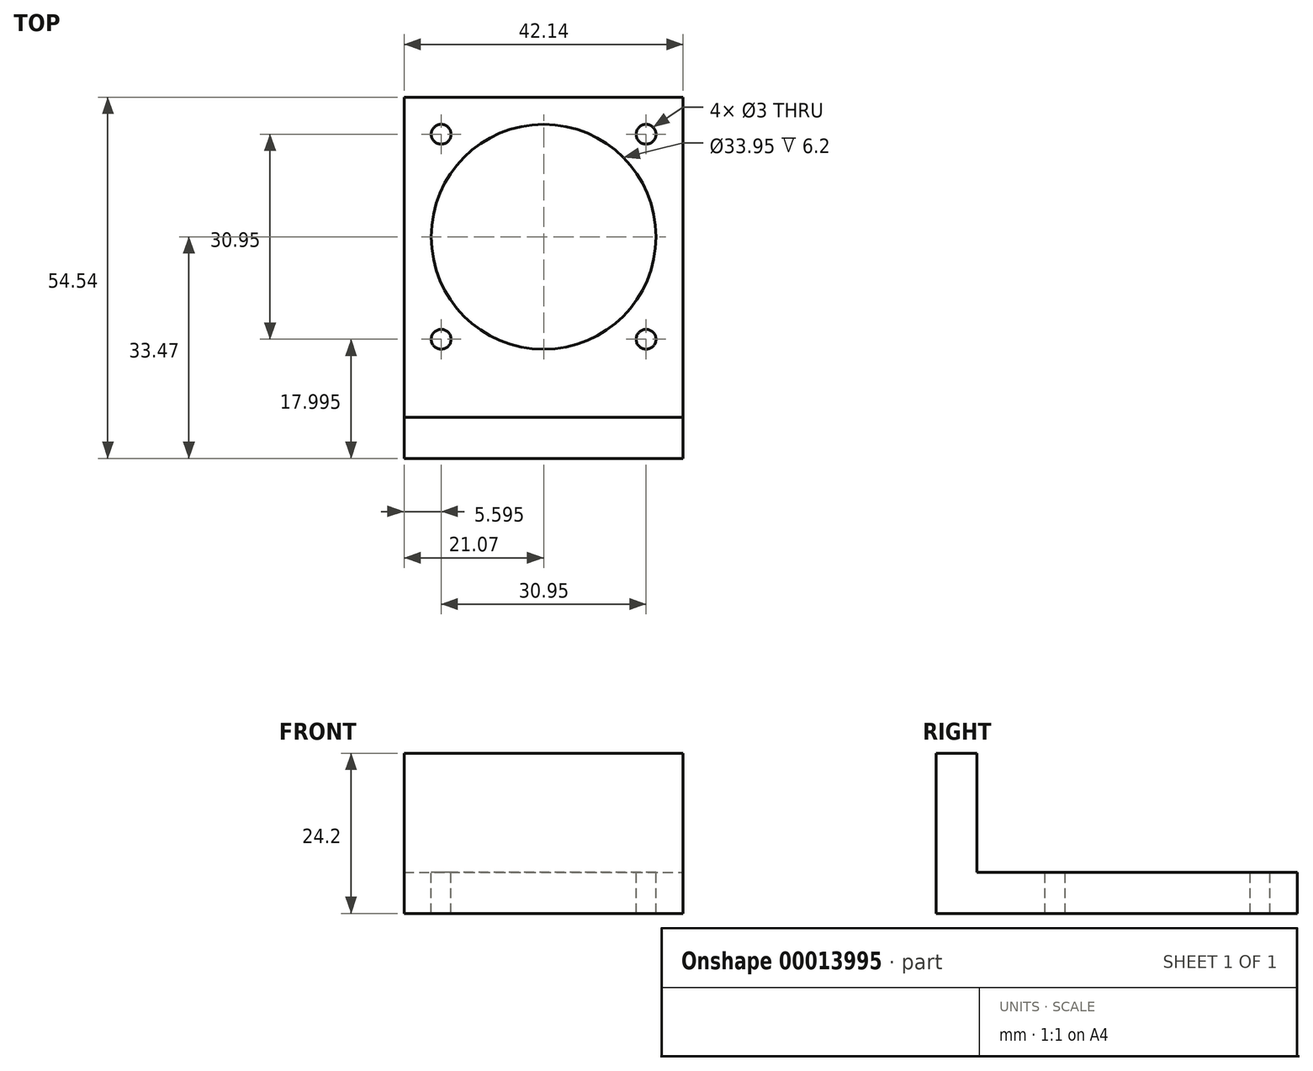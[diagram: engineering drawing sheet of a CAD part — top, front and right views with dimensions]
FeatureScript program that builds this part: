
annotation { "Feature Type Name" : "Feature", "Feature Type Description" : "" }
export const myFeature = defineFeature(function(context is Context, id is Id, definition is map)
    precondition{}
    {
        {
            var Q0;
            Q0=qCreatedBy(makeId("Top.planeOp"),FACE);
            var sketch = newSketch(context, id + "F0", { "sketchPlane" : qUnion([Q0])});
            skLineSegment(sketch, "E0.bottom", {"start": v(-21.07, 21.07) * mm, "end": v(0, 21.07) * mm});
            skLineSegment(sketch, "E0.top", {"start": v(-21.07, -21.07) * mm, "end": v(21.07, -21.07) * mm});
            skLineSegment(sketch, "E0.left", {"start": v(-21.08, 21.07) * mm, "end": v(-21.08, 0) * mm});
            skLineSegment(sketch, "E0.right", {"start": v(21.07, 21.07) * mm, "end": v(21.07, -21.07) * mm});
            skLineSegment(sketch, "E1", {"start": v(0, 63.85) * mm, "end": v(0, -67.06) * mm, "construction": true});
            skLineSegment(sketch, "E2", {"start": v(-87.9, 0) * mm, "end": v(96.2, 0) * mm, "construction": true});
            skLineSegment(sketch, "E3", {"start": v(0, 21.07) * mm, "end": v(21.07, 21.07) * mm});
            skLineSegment(sketch, "E4", {"start": v(-21.08, 0) * mm, "end": v(-21.08, -21.07) * mm});
            skCircle(sketch, "E5", {"center": v(-15.48, 15.47) * mm, "radius": 1.5 * mm});
            skCircle(sketch, "E6", {"center": v(15.48, 15.47) * mm, "radius": 1.5 * mm});
            skCircle(sketch, "E7", {"center": v(15.48, -15.48) * mm, "radius": 1.5 * mm});
            skCircle(sketch, "E8", {"center": v(-15.48, -15.48) * mm, "radius": 1.5 * mm});
            skLineSegment(sketch, "E9.bottom", {"start": v(-16.98, 16.97) * mm, "end": v(0, 16.97) * mm, "construction": true});
            skLineSegment(sketch, "E9.top", {"start": v(-16.98, -16.98) * mm, "end": v(16.98, -16.98) * mm, "construction": true});
            skLineSegment(sketch, "E9.left", {"start": v(-16.98, 16.97) * mm, "end": v(-16.98, 0) * mm, "construction": true});
            skLineSegment(sketch, "E9.right", {"start": v(16.98, 16.97) * mm, "end": v(16.98, -16.98) * mm, "construction": true});
            skLineSegment(sketch, "E10", {"start": v(0, 16.97) * mm, "end": v(16.98, 16.97) * mm, "construction": true});
            skLineSegment(sketch, "E11", {"start": v(-16.98, 0) * mm, "end": v(-16.98, -16.98) * mm, "construction": true});
            skLineSegment(sketch, "E12", {"start": v(-21.07, -21.07) * mm, "end": v(-21.07, -33.48) * mm});
            skLineSegment(sketch, "E13", {"start": v(-21.07, -33.48) * mm, "end": v(21.08, -33.48) * mm});
            skLineSegment(sketch, "E14", {"start": v(21.07, -33.47) * mm, "end": v(21.07, -21.07) * mm});
            skLineSegment(sketch, "E15", {"start": v(-21.08, -27.28) * mm, "end": v(21.08, -27.28) * mm});
            skCircle(sketch, "E16", {"center": v(0, 0) * mm, "radius": 16.98 * mm});
            skSolve(sketch);
        }
        {
            var Q0;
            Q0=makeQuery(id+"F0.imprint","IMPRINT",FACE,{"disambiguationData":[TD([[makeQuery(id+"F0.imprint","IMPRINT",EDGE,{"derivedFrom":sQuery(id+"F0.wireOp",EDGE,"E0.bottom")}),-1.0]])]});
            var Q1;
            {var subQ2=sQuery(id+"F0.wireOp",EDGE,"E0.top");Q1=makeQuery(id+"F0.imprint","IMPRINT",FACE,{"disambiguationData":[TD([[makeQuery(id+"F0.imprint","IMPRINT",EDGE,{"derivedFrom":subQ2}),-1.0]])]});}
            var Q2;
            {var subQ2=sQuery(id+"F0.wireOp",EDGE,"E13");Q2=makeQuery(id+"F0.imprint","IMPRINT",FACE,{"disambiguationData":[TD([[makeQuery(id+"F0.imprint","IMPRINT",EDGE,{"derivedFrom":subQ2}),1.0]])]});}
            extrude(context, id + "F1", {"entities" : qUnion([Q0, Q1, Q2]), "oppositeDirection" : true, "depth" : 6.2 * mm});
        }
        {
            var Q0;
            {var subQ2=sQuery(id+"F0.wireOp",EDGE,"E13");Q0=makeQuery(id+"F0.imprint","IMPRINT",FACE,{"disambiguationData":[TD([[makeQuery(id+"F0.imprint","IMPRINT",EDGE,{"derivedFrom":subQ2}),1.0]])]});}
            extrude(context, id + "F2", {"entities" : qUnion([Q0]), "operationType" : NewBodyOperationType.ADD, "depth" : 18 * mm});
        }
    });
